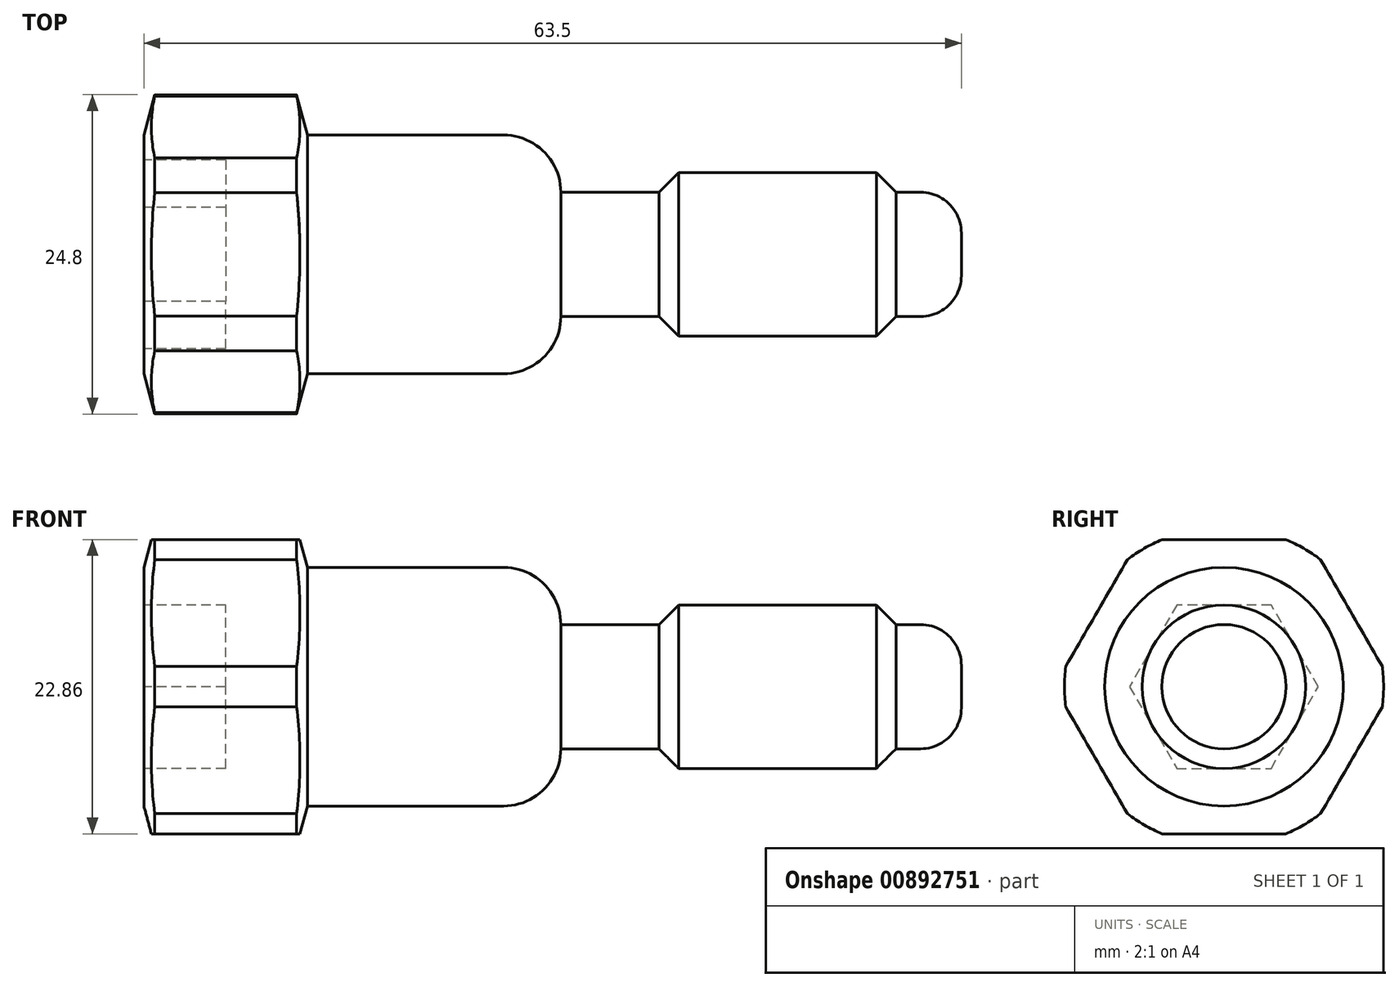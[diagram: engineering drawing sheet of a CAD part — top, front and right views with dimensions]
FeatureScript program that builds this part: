
annotation { "Feature Type Name" : "Feature", "Feature Type Description" : "" }
export const myFeature = defineFeature(function(context is Context, id is Id, definition is map)
    precondition{}
    {
        {
            var Q0;
            Q0=qCreatedBy(makeId("Front.planeOp"),FACE);
            var sketch = newSketch(context, id + "F0", { "sketchPlane" : qUnion([Q0])});
            skLineSegment(sketch, "E0", {"start": v(0, 0) * mm, "end": v(-63.5, 0) * mm});
            skLineSegment(sketch, "E1", {"start": v(0, 0) * mm, "end": v(0, 1.65) * mm});
            skLineSegment(sketch, "E2", {"start": v(-3.18, 4.83) * mm, "end": v(-5.08, 4.83) * mm});
            skLineSegment(sketch, "E3", {"start": v(-5.08, 4.83) * mm, "end": v(-6.6, 6.35) * mm});
            skLineSegment(sketch, "E4", {"start": v(-6.6, 6.35) * mm, "end": v(-21.97, 6.35) * mm});
            skLineSegment(sketch, "E5", {"start": v(-21.97, 6.35) * mm, "end": v(-23.5, 4.83) * mm});
            skLineSegment(sketch, "E6", {"start": v(-23.5, 4.83) * mm, "end": v(-31.12, 4.83) * mm});
            skLineSegment(sketch, "E7", {"start": v(-31.12, 4.83) * mm, "end": v(-31.12, 4.83) * mm});
            skLineSegment(sketch, "E8", {"start": v(-35.56, 9.27) * mm, "end": v(-50.8, 9.27) * mm});
            skPoint(sketch, "E9.visualSharp", {"position": v(0, 4.83) * mm});
            skArc(sketch, "E9.filletArc", {"start": v(0, 1.65) * mm, "mid": v(-0.93, 3.9) * mm, "end": v(-3.18, 4.83) * mm});
            skPoint(sketch, "E10.visualSharp", {"position": v(-31.12, 9.27) * mm});
            skArc(sketch, "E10.filletArc", {"start": v(-31.12, 4.83) * mm, "mid": v(-32.42, 7.97) * mm, "end": v(-35.56, 9.27) * mm});
            skLineSegment(sketch, "E11", {"start": v(-50.8, 9.27) * mm, "end": v(-51.64, 12.4) * mm});
            skLineSegment(sketch, "E12", {"start": v(-51.64, 12.4) * mm, "end": v(-62.66, 12.4) * mm});
            skLineSegment(sketch, "E13", {"start": v(-62.66, 12.4) * mm, "end": v(-63.5, 9.27) * mm});
            skLineSegment(sketch, "E14", {"start": v(-63.5, 9.27) * mm, "end": v(-63.5, 0) * mm});
            skSolve(sketch);
        }
        {
            var Q0;
            Q0 = qSketchRegion(id + "F0", true);
            var Q1;
            Q1=sQuery(id+"F0.wireOp",EDGE,"E0");
            revolve(context, id + "F1", {"surfaceOperationType" : NewSurfaceOperationType.NEW, "entities" : qUnion([Q0]), "axis" : qUnion([Q1]), "revolveType" : RevolveType.FULL});
        }
        {
            var Q0;
            Q0=makeQuery(id+"F1.opRevolve","SWEPT_FACE",FACE,{"disambiguationData":[OSD([sQuery(id+"F0.wireOp",EDGE,"E14")])]});
            var sketch = newSketch(context, id + "F2", { "sketchPlane" : qUnion([Q0])});
            skCircle(sketch, "E15.cCircle", {"center": v(0, 0) * mm, "radius": 6.35 * mm, "construction": true});
            skLineSegment(sketch, "E15.0", {"start": v(-3.67, 6.35) * mm, "end": v(3.67, 6.35) * mm});
            skLineSegment(sketch, "E15.1", {"start": v(3.67, 6.35) * mm, "end": v(7.33, 0) * mm});
            skLineSegment(sketch, "E15.2", {"start": v(7.33, 0) * mm, "end": v(3.67, -6.35) * mm});
            skLineSegment(sketch, "E15.3", {"start": v(3.67, -6.35) * mm, "end": v(-3.67, -6.35) * mm});
            skLineSegment(sketch, "E15.4", {"start": v(-3.67, -6.35) * mm, "end": v(-7.33, 0) * mm});
            skLineSegment(sketch, "E15.5", {"start": v(-7.33, 0) * mm, "end": v(-3.67, 6.35) * mm});
            skPoint(sketch, "E15.0.midPoint", {"position": v(0, 6.35) * mm});
            skSolve(sketch);
        }
        {
            var Q0;
            Q0 = qSketchRegion(id + "F2", true);
            extrude(context, id + "F3", {"entities" : qUnion([Q0]), "operationType" : NewBodyOperationType.REMOVE, "oppositeDirection" : true, "depth" : 6.35 * mm, "offsetDistance" : 25.4 * mm});
        }
        {
            var Q0;
            Q0=makeQuery(id+"F1.opRevolve","SWEPT_FACE",FACE,{"disambiguationData":[OSD([sQuery(id+"F0.wireOp",EDGE,"E14")])]});
            var sketch = newSketch(context, id + "F4", { "sketchPlane" : qUnion([Q0])});
            skCircle(sketch, "E16.cCircle", {"center": v(0, 0) * mm, "radius": 11.43 * mm, "construction": true});
            skLineSegment(sketch, "E16.0", {"start": v(-6.6, 11.43) * mm, "end": v(6.6, 11.43) * mm});
            skLineSegment(sketch, "E16.1", {"start": v(6.6, 11.43) * mm, "end": v(13.2, 0) * mm});
            skLineSegment(sketch, "E16.2", {"start": v(13.2, 0) * mm, "end": v(6.6, -11.43) * mm});
            skLineSegment(sketch, "E16.3", {"start": v(6.6, -11.43) * mm, "end": v(-6.6, -11.43) * mm});
            skLineSegment(sketch, "E16.4", {"start": v(-6.6, -11.43) * mm, "end": v(-13.2, 0) * mm});
            skLineSegment(sketch, "E16.5", {"start": v(-13.2, 0) * mm, "end": v(-6.6, 11.43) * mm});
            skPoint(sketch, "E16.0.midPoint", {"position": v(0, 11.43) * mm});
            skCircle(sketch, "E17", {"center": v(0, 0) * mm, "radius": 15.61 * mm});
            skSolve(sketch);
        }
        {
            var Q0;
            Q0 = qSketchRegion(id + "F4", true);
            extrude(context, id + "F5", {"entities" : qUnion([Q0]), "operationType" : NewBodyOperationType.REMOVE, "oppositeDirection" : true, "depth" : 25.4 * mm, "offsetDistance" : 25.4 * mm});
        }
    });
